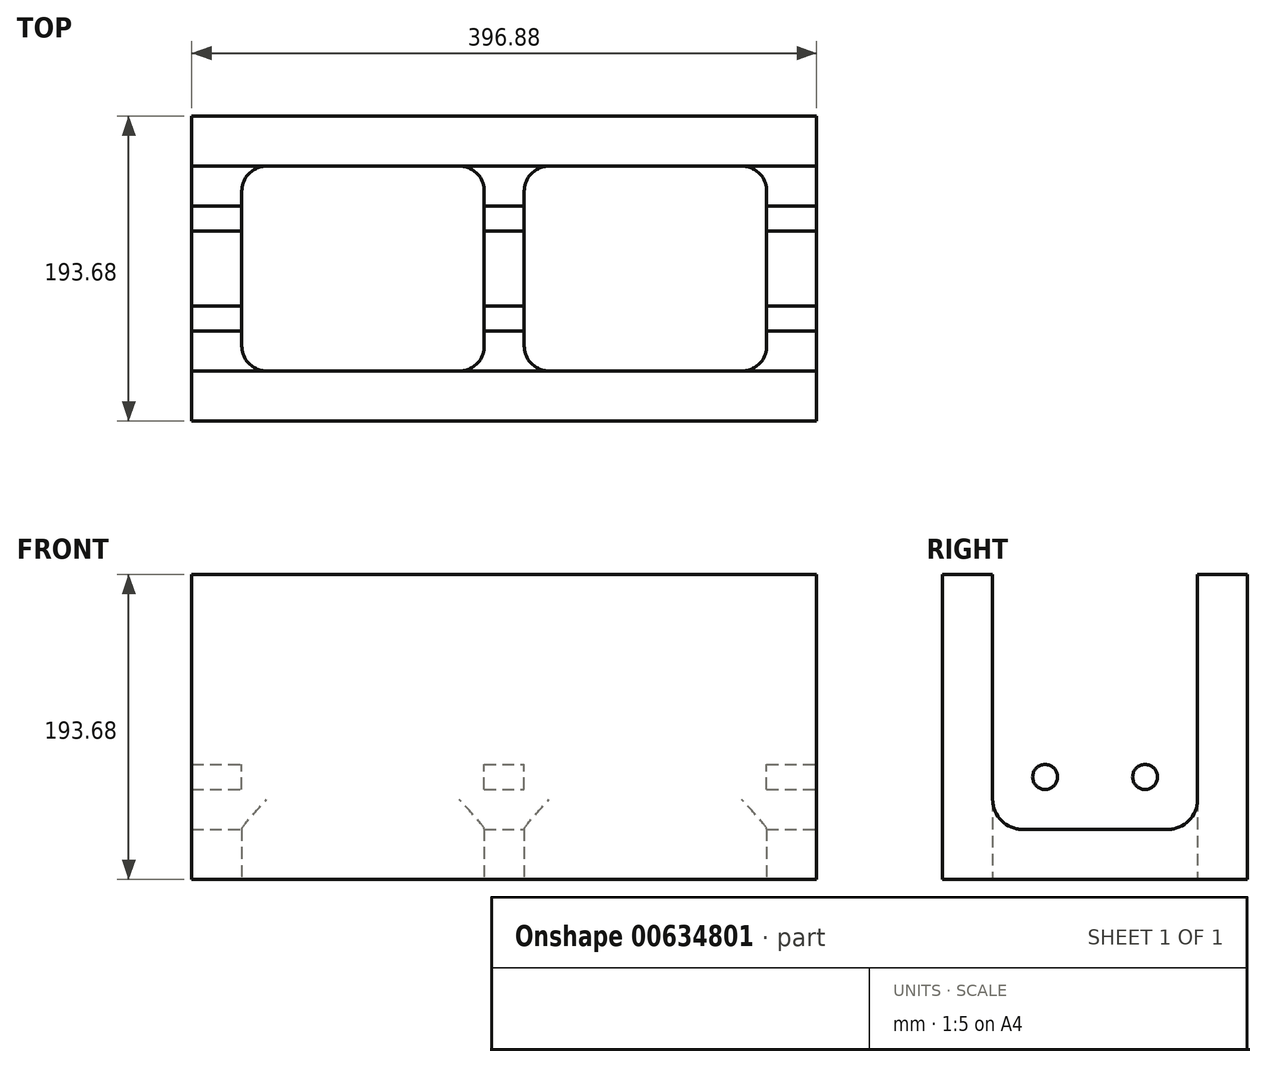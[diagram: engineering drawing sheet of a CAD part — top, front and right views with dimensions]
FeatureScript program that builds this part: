
annotation { "Feature Type Name" : "Feature", "Feature Type Description" : "" }
export const myFeature = defineFeature(function(context is Context, id is Id, definition is map)
    precondition{}
    {
        {
            var Q0;
            Q0=qCreatedBy(makeId("Top.planeOp"),FACE);
            var sketch = newSketch(context, id + "F0", { "sketchPlane" : qUnion([Q0])});
            skLineSegment(sketch, "E0.bottom", {"start": v(-198.44, 96.84) * mm, "end": v(198.44, 96.84) * mm});
            skLineSegment(sketch, "E0.top", {"start": v(-198.44, -96.84) * mm, "end": v(198.44, -96.84) * mm});
            skLineSegment(sketch, "E0.left", {"start": v(-198.44, 96.84) * mm, "end": v(-198.44, -96.84) * mm});
            skLineSegment(sketch, "E0.right", {"start": v(198.44, 96.84) * mm, "end": v(198.44, -96.84) * mm});
            skLineSegment(sketch, "E1.bottom", {"start": v(-150.81, 65.09) * mm, "end": v(-28.57, 65.09) * mm});
            skLineSegment(sketch, "E1.top", {"start": v(-150.81, -65.09) * mm, "end": v(-28.58, -65.09) * mm});
            skLineSegment(sketch, "E1.left", {"start": v(-166.69, 49.21) * mm, "end": v(-166.69, -49.21) * mm});
            skLineSegment(sketch, "E1.right", {"start": v(-12.7, 49.21) * mm, "end": v(-12.7, -49.21) * mm});
            skLineSegment(sketch, "E2", {"start": v(0, 96.84) * mm, "end": v(0, -96.84) * mm, "construction": true});
            skLineSegment(sketch, "E3.MirrorCS", {"start": v(166.69, 49.21) * mm, "end": v(166.69, -49.21) * mm});
            skLineSegment(sketch, "E4.MirrorCS", {"start": v(150.81, 65.09) * mm, "end": v(28.57, 65.09) * mm});
            skLineSegment(sketch, "E5.MirrorCS", {"start": v(150.81, -65.09) * mm, "end": v(28.57, -65.09) * mm});
            skLineSegment(sketch, "E6.MirrorCS", {"start": v(12.7, 49.21) * mm, "end": v(12.7, -49.21) * mm});
            skPoint(sketch, "E7.visualSharp", {"position": v(-166.69, 65.09) * mm});
            skArc(sketch, "E7.filletArc", {"start": v(-150.81, 65.09) * mm, "mid": v(-162.04, 60.44) * mm, "end": v(-166.69, 49.21) * mm});
            skPoint(sketch, "E8.visualSharp", {"position": v(-166.69, -65.09) * mm});
            skArc(sketch, "E8.filletArc", {"start": v(-166.69, -49.21) * mm, "mid": v(-162.04, -60.44) * mm, "end": v(-150.81, -65.09) * mm});
            skPoint(sketch, "E9.visualSharp", {"position": v(-12.7, -65.09) * mm});
            skArc(sketch, "E9.filletArc", {"start": v(-28.58, -65.09) * mm, "mid": v(-17.35, -60.44) * mm, "end": v(-12.7, -49.21) * mm});
            skPoint(sketch, "E10.visualSharp", {"position": v(-12.7, 65.09) * mm});
            skArc(sketch, "E10.filletArc", {"start": v(-12.7, 49.21) * mm, "mid": v(-17.35, 60.44) * mm, "end": v(-28.57, 65.09) * mm});
            skPoint(sketch, "E11.visualSharp", {"position": v(12.7, 65.09) * mm});
            skArc(sketch, "E11.filletArc", {"start": v(28.57, 65.09) * mm, "mid": v(17.35, 60.44) * mm, "end": v(12.7, 49.21) * mm});
            skPoint(sketch, "E12.visualSharp", {"position": v(12.7, -65.09) * mm});
            skArc(sketch, "E12.filletArc", {"start": v(12.7, -49.21) * mm, "mid": v(17.35, -60.44) * mm, "end": v(28.57, -65.09) * mm});
            skPoint(sketch, "E13.visualSharp", {"position": v(166.69, -65.09) * mm});
            skArc(sketch, "E13.filletArc", {"start": v(150.81, -65.09) * mm, "mid": v(162.04, -60.44) * mm, "end": v(166.69, -49.21) * mm});
            skPoint(sketch, "E14.visualSharp", {"position": v(166.69, 65.09) * mm});
            skArc(sketch, "E14.filletArc", {"start": v(166.69, 49.21) * mm, "mid": v(162.04, 60.44) * mm, "end": v(150.81, 65.09) * mm});
            skLineSegment(sketch, "E15", {"start": v(-12.7, 0) * mm, "end": v(12.7, 0) * mm});
            skSolve(sketch);
        }
        {
            var Q0;
            Q0=makeQuery(id+"F0.imprint","IMPRINT",FACE,{"disambiguationData":[TD([[makeQuery(id+"F0.imprint","IMPRINT",EDGE,{"derivedFrom":sQuery(id+"F0.wireOp",EDGE,"E0.bottom")}),-1.0]])]});
            extrude(context, id + "F1", {"entities" : qUnion([Q0]), "endBound" : BoundingType.SYMMETRIC, "depth" : 193.67 * mm, "offsetDistance" : 25.4 * mm});
        }
        {
            var Q0;
            Q0=makeQuery(id+"F1.opExtrude","SWEPT_FACE",FACE,{"disambiguationData":[OSD([sQuery(id+"F0.wireOp",EDGE,"E0.right")])]});
            var sketch = newSketch(context, id + "F2", { "sketchPlane" : qUnion([Q0])});
            skLineSegment(sketch, "E16", {"start": v(-65.09, 96.84) * mm, "end": v(-65.09, -46.04) * mm});
            skLineSegment(sketch, "E17", {"start": v(-46.04, -65.09) * mm, "end": v(46.04, -65.09) * mm});
            skLineSegment(sketch, "E18", {"start": v(65.09, -46.04) * mm, "end": v(65.09, 96.84) * mm});
            skLineSegment(sketch, "E19", {"start": v(65.09, 96.84) * mm, "end": v(-65.09, 96.84) * mm});
            skLineSegment(sketch, "E20", {"start": v(0, -65.09) * mm, "end": v(0, -96.84) * mm, "construction": true});
            skPoint(sketch, "E21.visualSharp", {"position": v(-65.09, -65.09) * mm});
            skArc(sketch, "E21.filletArc", {"start": v(-65.09, -46.04) * mm, "mid": v(-59.5, -59.5) * mm, "end": v(-46.04, -65.09) * mm});
            skPoint(sketch, "E22.visualSharp", {"position": v(65.09, -65.09) * mm});
            skArc(sketch, "E22.filletArc", {"start": v(46.04, -65.09) * mm, "mid": v(59.5, -59.5) * mm, "end": v(65.09, -46.04) * mm});
            skLineSegment(sketch, "E23", {"start": v(65.09, 25.4) * mm, "end": v(96.84, 25.4) * mm, "construction": true});
            skCircle(sketch, "E24", {"center": v(-31.75, -31.75) * mm, "radius": 7.94 * mm});
            skCircle(sketch, "E25", {"center": v(31.75, -31.75) * mm, "radius": 7.94 * mm});
            skSolve(sketch);
        }
        {
            var Q0;
            Q0 = qSketchRegion(id + "F2", true);
            extrude(context, id + "F3", {"entities" : qUnion([Q0]), "operationType" : NewBodyOperationType.REMOVE, "endBound" : BoundingType.THROUGH_ALL, "oppositeDirection" : true, "depth" : 25.4 * mm, "offsetDistance" : 25.4 * mm});
        }
    });
